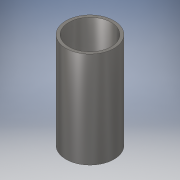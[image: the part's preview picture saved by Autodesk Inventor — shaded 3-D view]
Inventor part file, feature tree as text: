
AUTODESK INVENTOR PART (.ipt)
format: ipt  version: 2018 (Build 220112000, 112)  size: 102,912 bytes
history: native  units: in
note: dims shown in document units (in); Inventor stores cm internally (conversion verified against a paired STEP export)
features: extrude x1, sketch x1
ambient origin geometry x8: Origin, YZ Plane, XZ Plane, XY Plane, X Axis, Y Axis, Z Axis, Center Point
bodies: Solid1 (feature_tree)
feature tree (2):
  extrude  "Extrusion1"  Depth=1.0in
  sketch  "Sketch1"  dims[d0=0.5in d1=0.03in d2=1.0in d3=0.0in]
